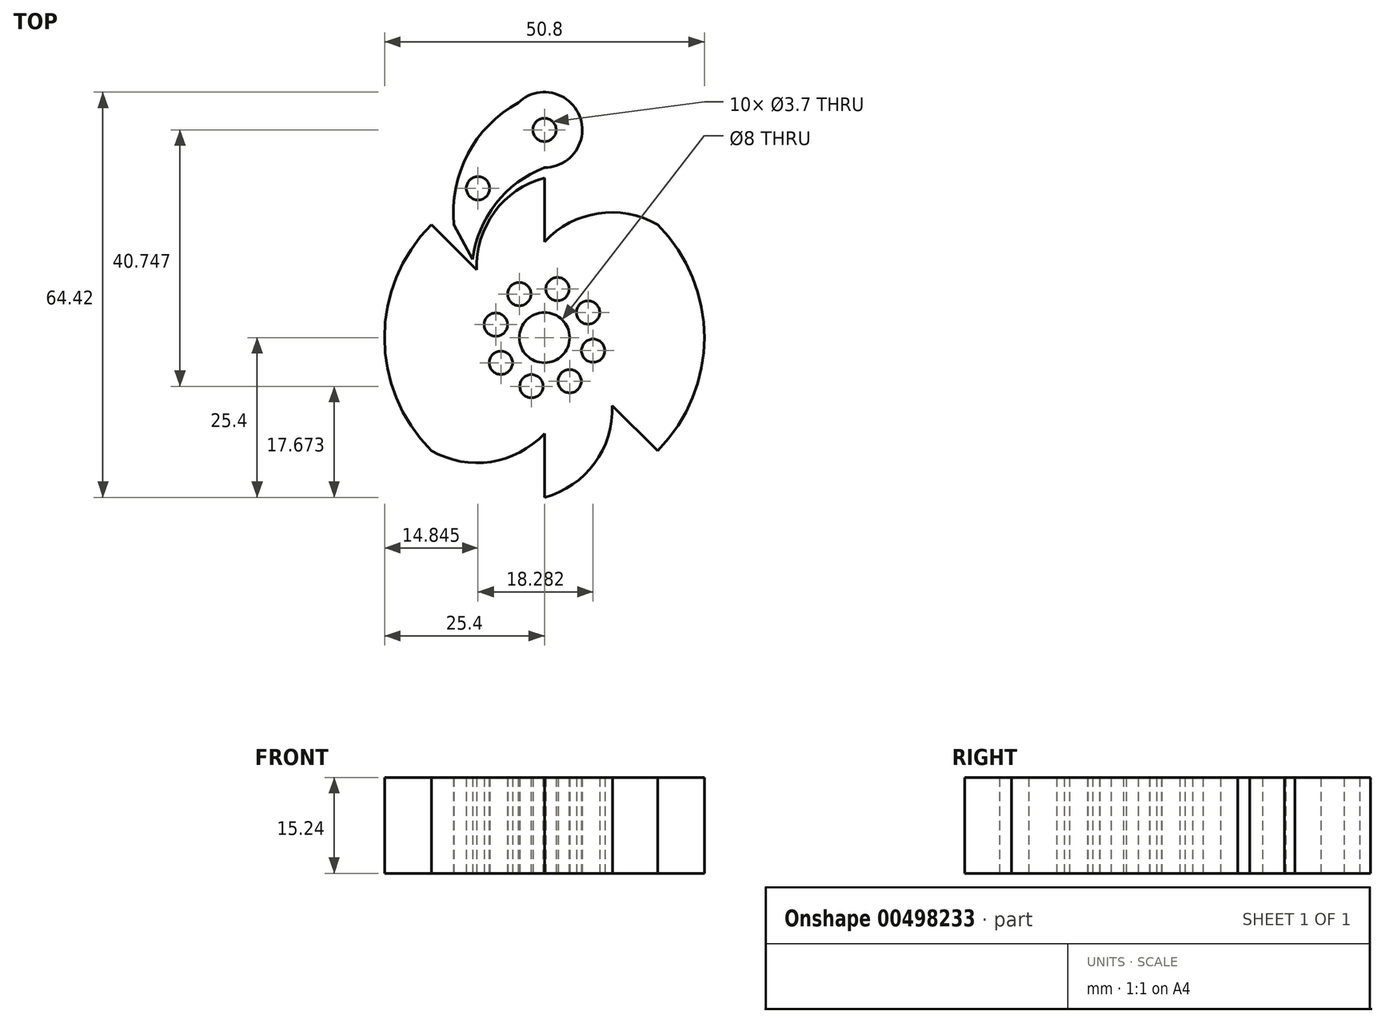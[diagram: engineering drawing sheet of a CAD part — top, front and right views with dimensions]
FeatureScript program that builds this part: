
annotation { "Feature Type Name" : "Feature", "Feature Type Description" : "" }
export const myFeature = defineFeature(function(context is Context, id is Id, definition is map)
    precondition{}
    {
        {
            var Q0;
            Q0=qCreatedBy(makeId("Top.planeOp"),FACE);
            var sketch = newSketch(context, id + "F0", { "sketchPlane" : qUnion([Q0])});
            skPoint(sketch, "E0", {"position": v(0, 25.4) * mm});
            skPoint(sketch, "E1", {"position": v(0, 15.24) * mm});
            skLineSegment(sketch, "E2", {"start": v(0, 25.4) * mm, "end": v(0, 15.24) * mm});
            skLineSegment(sketch, "E3.1.0", {"start": v(-17.96, 17.96) * mm, "end": v(-10.78, 10.78) * mm});
            skPoint(sketch, "E3.1.1", {"position": v(-17.96, 17.96) * mm});
            skLineSegment(sketch, "E3.2.0", {"start": v(-25.4, 0) * mm, "end": v(-15.24, 0) * mm});
            skPoint(sketch, "E3.2.1", {"position": v(-25.4, 0) * mm});
            skLineSegment(sketch, "E3.3.0", {"start": v(-17.96, -17.96) * mm, "end": v(-10.78, -10.78) * mm});
            skPoint(sketch, "E3.3.1", {"position": v(-17.96, -17.96) * mm});
            skLineSegment(sketch, "E3.4.0", {"start": v(0, -25.4) * mm, "end": v(0, -15.24) * mm});
            skPoint(sketch, "E3.4.1", {"position": v(0, -25.4) * mm});
            skLineSegment(sketch, "E3.5.0", {"start": v(17.96, -17.96) * mm, "end": v(10.78, -10.78) * mm});
            skPoint(sketch, "E3.5.1", {"position": v(17.96, -17.96) * mm});
            skLineSegment(sketch, "E3.6.0", {"start": v(25.4, 0) * mm, "end": v(15.24, 0) * mm});
            skPoint(sketch, "E3.6.1", {"position": v(25.4, 0) * mm});
            skLineSegment(sketch, "E3.7.0", {"start": v(17.96, 17.96) * mm, "end": v(10.78, 10.78) * mm});
            skPoint(sketch, "E3.7.1", {"position": v(17.96, 17.96) * mm});
            skPoint(sketch, "E3.center", {"position": v(0, 0) * mm});
            skPoint(sketch, "E4.center", {"position": v(2.54, 2.54) * mm});
            skCircle(sketch, "E5", {"center": v(0, 0) * mm, "radius": 4 * mm});
            skPoint(sketch, "E6.orphan", {"position": v(-10.16, 0) * mm});
            skPoint(sketch, "E7.orphan", {"position": v(-8.24, 9.72) * mm});
            skPoint(sketch, "E8.orphan", {"position": v(24.35, 2.54) * mm});
            skPoint(sketch, "E9.orphan", {"position": v(15.24, 5.08) * mm});
            skPoint(sketch, "E10.orphan", {"position": v(13.32, -4.64) * mm});
            skPoint(sketch, "E11.orphan", {"position": v(-4.64, -8.24) * mm});
            skArc(sketch, "E12", {"start": v(-17.96, 17.96) * mm, "mid": v(-19.74, 8.5) * mm, "end": v(-15.24, 0) * mm});
            skArc(sketch, "E13.1.0", {"start": v(-25.4, 0) * mm, "mid": v(-19.97, -7.95) * mm, "end": v(-10.78, -10.78) * mm});
            skArc(sketch, "E13.2.0", {"start": v(-17.96, -17.96) * mm, "mid": v(-8.5, -19.74) * mm, "end": v(0, -15.24) * mm});
            skArc(sketch, "E13.3.0", {"start": v(0, -25.4) * mm, "mid": v(7.95, -19.97) * mm, "end": v(10.78, -10.78) * mm});
            skArc(sketch, "E13.4.0", {"start": v(17.96, -17.96) * mm, "mid": v(19.74, -8.5) * mm, "end": v(15.24, 0) * mm});
            skArc(sketch, "E13.5.0", {"start": v(25.4, 0) * mm, "mid": v(19.97, 7.95) * mm, "end": v(10.78, 10.78) * mm});
            skArc(sketch, "E13.6.0", {"start": v(17.96, 17.96) * mm, "mid": v(8.5, 19.74) * mm, "end": v(0, 15.24) * mm});
            skArc(sketch, "E13.7.0", {"start": v(0, 25.4) * mm, "mid": v(-7.95, 19.97) * mm, "end": v(-10.78, 10.78) * mm});
            skCircle(sketch, "E14", {"center": v(0, 33.02) * mm, "radius": 6 * mm});
            skPoint(sketch, "E15.orphan", {"position": v(-14.37, 14.37) * mm});
            skPoint(sketch, "E16.start.orphan", {"position": v(0, 39.02) * mm});
            skPoint(sketch, "E17.start.orphan", {"position": v(0, 27.02) * mm});
            skArc(sketch, "E18", {"start": v(0, 27.02) * mm, "mid": v(-7.72, 21.3) * mm, "end": v(-11.42, 12.44) * mm});
            skArc(sketch, "E19", {"start": v(-4.19, 37.32) * mm, "mid": v(-12.2, 29.17) * mm, "end": v(-14.37, 17.96) * mm});
            skLineSegment(sketch, "E20", {"start": v(-14.37, 17.96) * mm, "end": v(-11.42, 12.44) * mm});
            skCircle(sketch, "E21", {"center": v(0, 33.02) * mm, "radius": 1.85 * mm});
            skArc(sketch, "E22", {"start": v(-17.96, 17.96) * mm, "mid": v(-25.4, 0) * mm, "end": v(-17.96, -17.96) * mm});
            skCircle(sketch, "E23", {"center": v(-10.55, 23.74) * mm, "radius": 1.85 * mm});
            skArc(sketch, "E24.trimOffspring", {"start": v(17.96, -17.96) * mm, "mid": v(25.4, 0) * mm, "end": v(17.96, 17.96) * mm});
            skCircle(sketch, "E25", {"center": v(2.07, 7.73) * mm, "radius": 1.85 * mm});
            skCircle(sketch, "E26.1.0", {"center": v(-4, 6.93) * mm, "radius": 1.85 * mm});
            skCircle(sketch, "E26.2.0", {"center": v(-7.73, 2.07) * mm, "radius": 1.85 * mm});
            skCircle(sketch, "E26.3.0", {"center": v(-6.93, -4) * mm, "radius": 1.85 * mm});
            skCircle(sketch, "E26.4.0", {"center": v(-2.07, -7.73) * mm, "radius": 1.85 * mm});
            skCircle(sketch, "E26.5.0", {"center": v(4, -6.93) * mm, "radius": 1.85 * mm});
            skCircle(sketch, "E26.6.0", {"center": v(7.73, -2.07) * mm, "radius": 1.85 * mm});
            skCircle(sketch, "E26.7.0", {"center": v(6.93, 4) * mm, "radius": 1.85 * mm});
            skLineSegment(sketch, "E27.trimOffspring", {"start": v(0, 15.24) * mm, "end": v(0, 56.83) * mm});
            skSolve(sketch);
        }
        {
            var Q0;
            Q0 = qSketchRegion(id + "F0", true);
            extrude(context, id + "F1", {"entities" : qUnion([Q0]), "depth" : 15.24 * mm});
        }
    });
